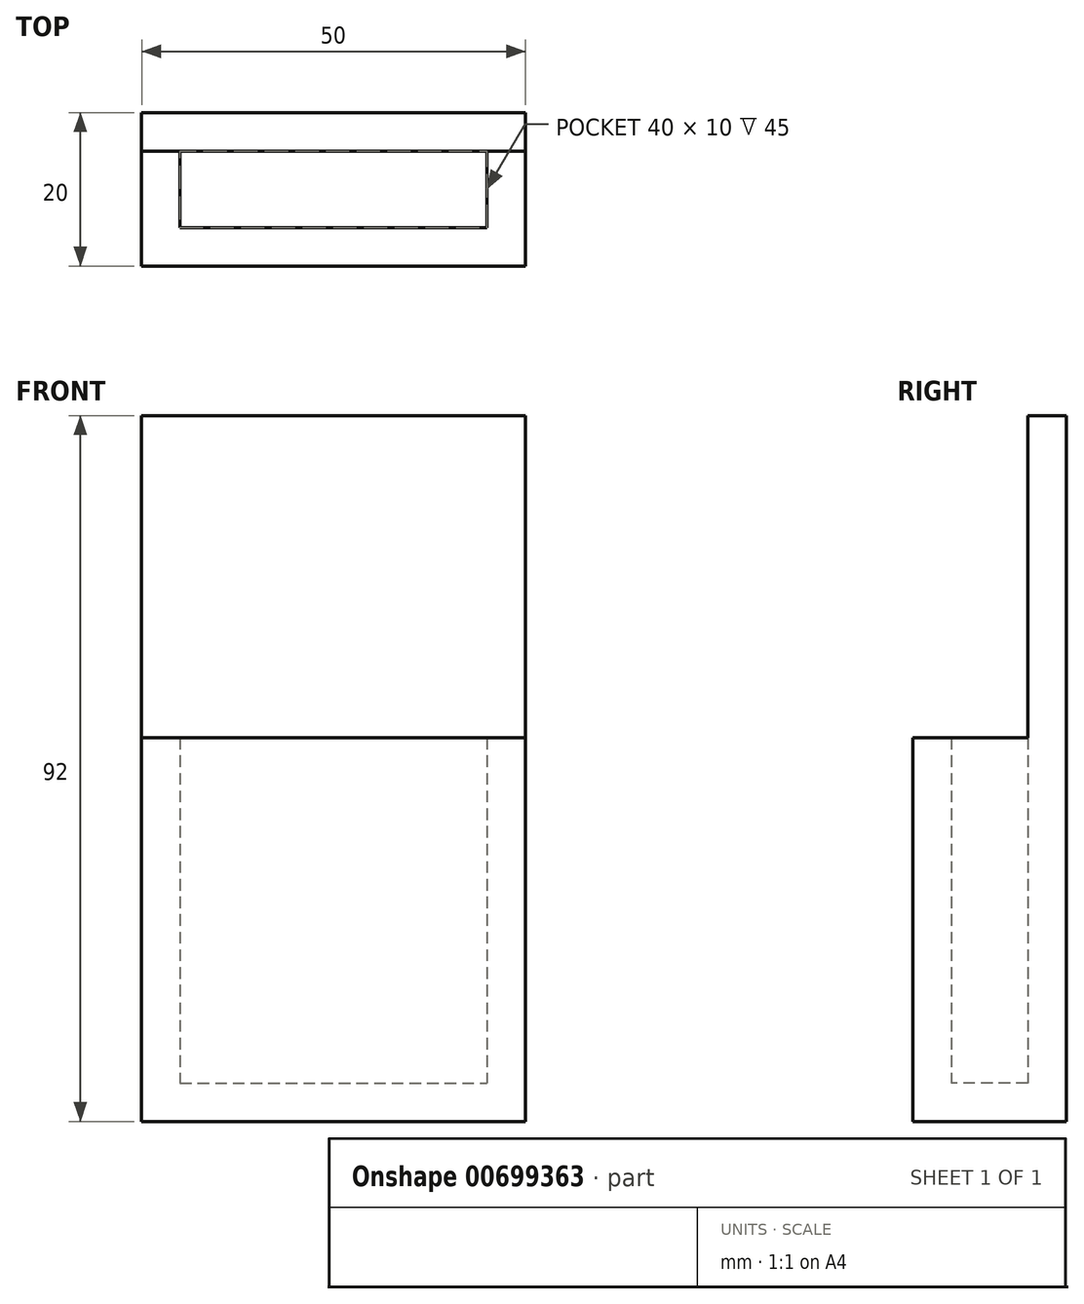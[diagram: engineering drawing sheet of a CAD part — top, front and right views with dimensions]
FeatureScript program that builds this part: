
annotation { "Feature Type Name" : "Feature", "Feature Type Description" : "" }
export const myFeature = defineFeature(function(context is Context, id is Id, definition is map)
    precondition{}
    {
        {
            var Q0;
            Q0=qCreatedBy(makeId("Top.planeOp"),FACE);
            var sketch = newSketch(context, id + "F0", { "sketchPlane" : qUnion([Q0])});
            skLineSegment(sketch, "E0.bottom", {"start": v(-21.22, 12.05) * mm, "end": v(18.78, 12.05) * mm});
            skLineSegment(sketch, "E0.top", {"start": v(-21.22, 2.05) * mm, "end": v(18.78, 2.05) * mm});
            skLineSegment(sketch, "E0.left", {"start": v(-21.22, 12.05) * mm, "end": v(-21.22, 2.05) * mm});
            skLineSegment(sketch, "E0.right", {"start": v(18.78, 12.05) * mm, "end": v(18.78, 2.05) * mm});
            skLineSegment(sketch, "E1.bottom", {"start": v(-26.22, 17.05) * mm, "end": v(23.78, 17.05) * mm});
            skLineSegment(sketch, "E1.top", {"start": v(-26.22, -2.95) * mm, "end": v(23.78, -2.95) * mm});
            skLineSegment(sketch, "E1.left", {"start": v(-26.22, 17.05) * mm, "end": v(-26.22, -2.95) * mm});
            skLineSegment(sketch, "E1.right", {"start": v(23.78, 17.05) * mm, "end": v(23.78, -2.95) * mm});
            skLineSegment(sketch, "E2", {"start": v(-21.22, 12.05) * mm, "end": v(-26.22, 12.05) * mm});
            skLineSegment(sketch, "E3", {"start": v(18.78, 12.05) * mm, "end": v(23.78, 12.05) * mm});
            skSolve(sketch);
        }
        {
            var Q0;
            Q0=makeQuery(id+"F0.imprint","IMPRINT",FACE,{"disambiguationData":[TD([[makeQuery(id+"F0.imprint","IMPRINT",EDGE,{"derivedFrom":sQuery(id+"F0.wireOp",EDGE,"E0.bottom")}),-1.0]])]});
            extrude(context, id + "F1", {"entities" : qUnion([Q0]), "depth" : 5 * mm, "offsetDistance" : 25 * mm});
        }
        {
            var Q0;
            Q0=makeQuery(id+"F0.imprint","IMPRINT",FACE,{"disambiguationData":[TD([[makeQuery(id+"F0.imprint","IMPRINT",EDGE,{"derivedFrom":sQuery(id+"F0.wireOp",EDGE,"E0.bottom")}),1.0]])]});
            extrude(context, id + "F2", {"entities" : qUnion([Q0]), "operationType" : NewBodyOperationType.ADD, "depth" : 92 * mm, "offsetDistance" : 25 * mm});
        }
        {
            var Q0;
            Q0=makeQuery(id+"F0.imprint","IMPRINT",FACE,{"disambiguationData":[TD([[makeQuery(id+"F0.imprint","IMPRINT",EDGE,{"derivedFrom":sQuery(id+"F0.wireOp",EDGE,"E0.top")}),-1.0]])]});
            extrude(context, id + "F3", {"entities" : qUnion([Q0]), "operationType" : NewBodyOperationType.ADD, "depth" : 50 * mm, "offsetDistance" : 25 * mm});
        }
    });
